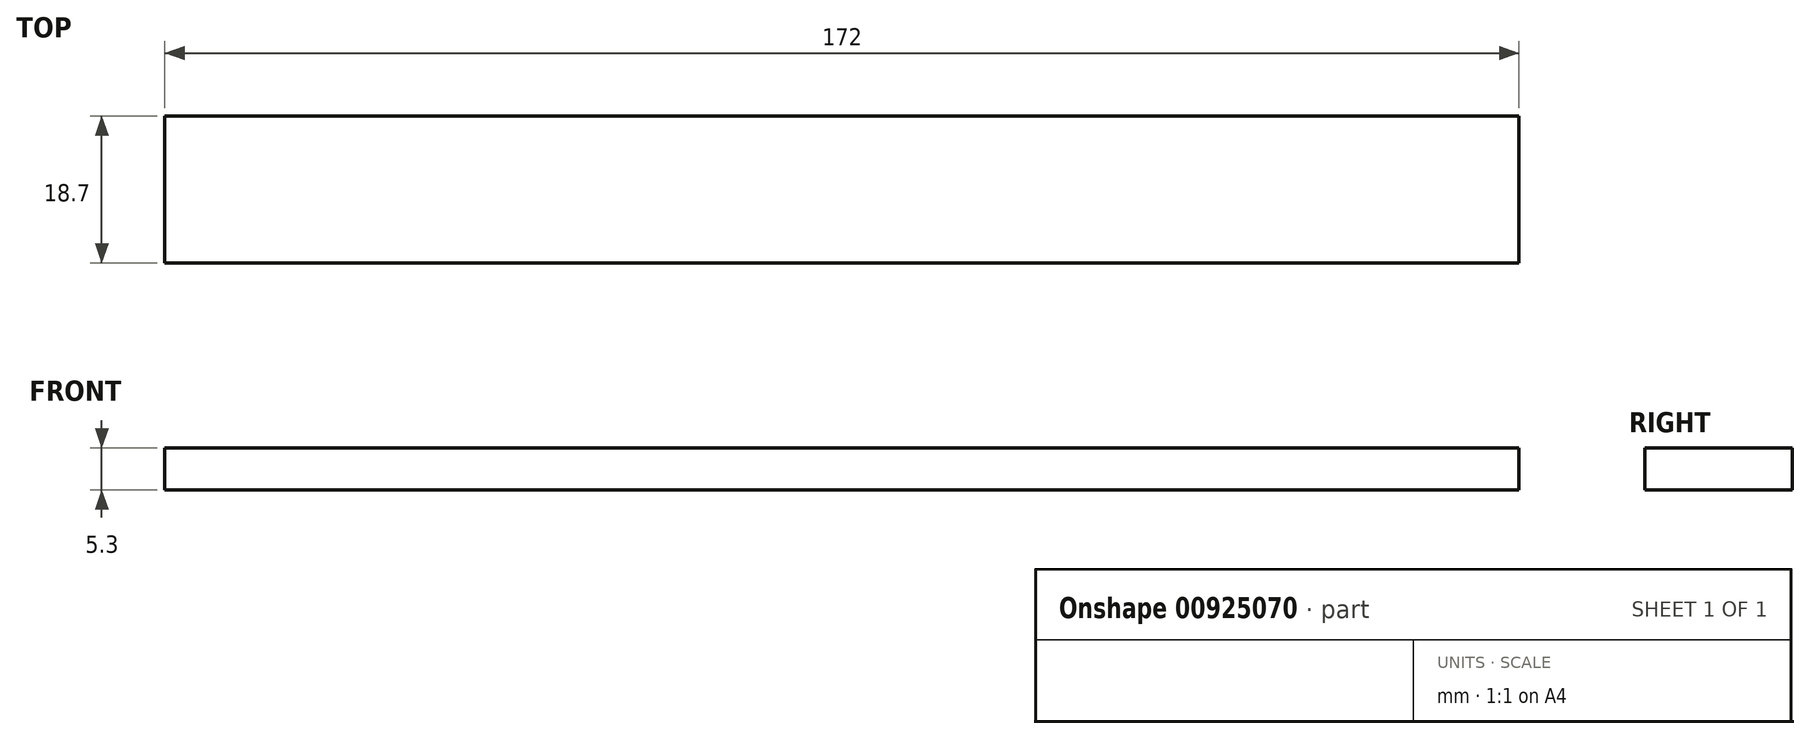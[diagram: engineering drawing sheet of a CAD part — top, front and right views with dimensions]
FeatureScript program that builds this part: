
annotation { "Feature Type Name" : "Feature", "Feature Type Description" : "" }
export const myFeature = defineFeature(function(context is Context, id is Id, definition is map)
    precondition{}
    {
        {
            var Q0;
            Q0=qCreatedBy(makeId("Top.planeOp"),FACE);
            var sketch = newSketch(context, id + "F0", { "sketchPlane" : qUnion([Q0])});
            skLineSegment(sketch, "E0.bottom", {"start": v(86, 9.35) * mm, "end": v(-86, 9.35) * mm});
            skLineSegment(sketch, "E0.top", {"start": v(86, -9.35) * mm, "end": v(-86, -9.35) * mm});
            skLineSegment(sketch, "E0.left", {"start": v(86, 9.35) * mm, "end": v(86, -9.35) * mm});
            skLineSegment(sketch, "E0.right", {"start": v(-86, 9.35) * mm, "end": v(-86, -9.35) * mm});
            skPoint(sketch, "E0.middle", {"position": v(0, 0) * mm});
            skSolve(sketch);
        }
        {
            var Q0;
            Q0 = qSketchRegion(id + "F0", true);
            extrude(context, id + "F1", {"entities" : qUnion([Q0]), "endBound" : BoundingType.SYMMETRIC, "depth" : 5.3 * mm, "offsetDistance" : 25 * mm});
        }
    });
